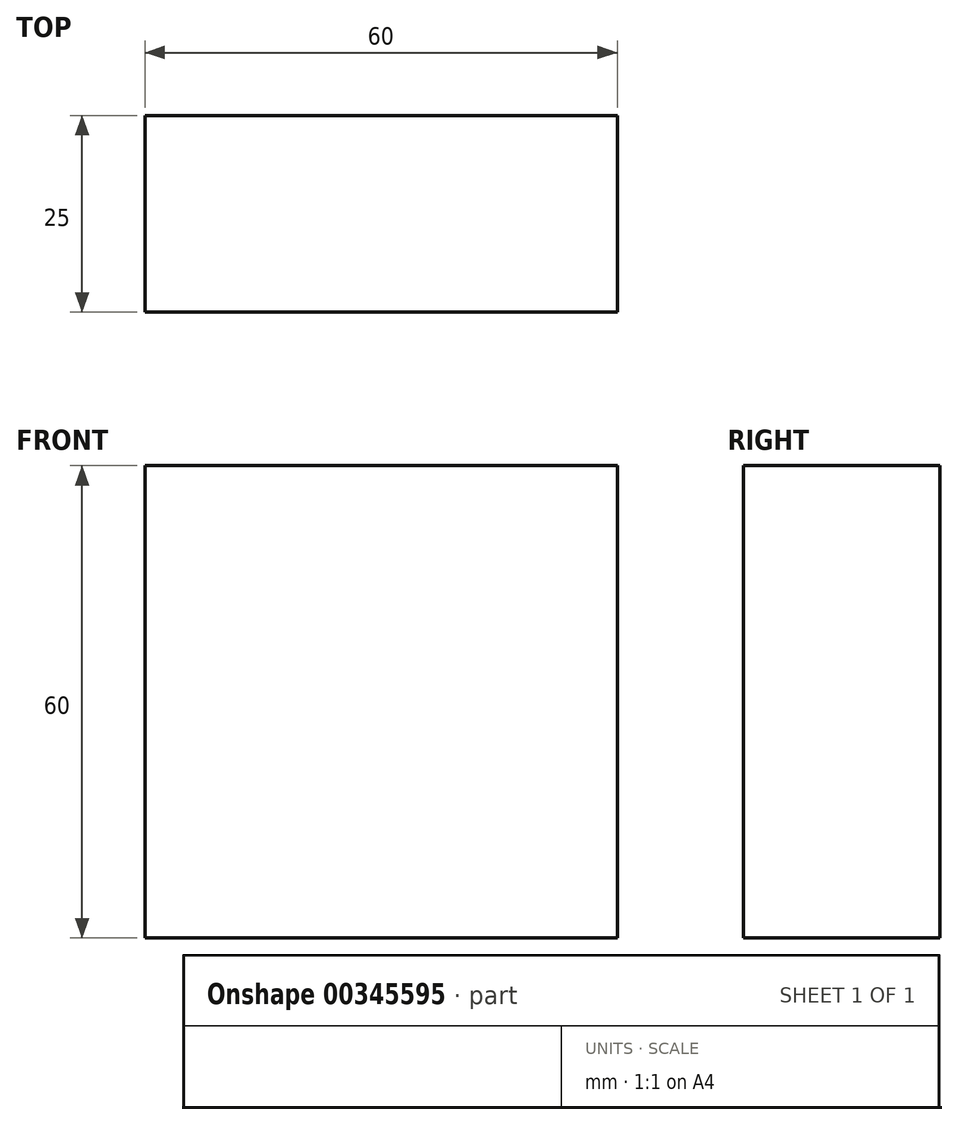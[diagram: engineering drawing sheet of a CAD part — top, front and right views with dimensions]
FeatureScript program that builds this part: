
annotation { "Feature Type Name" : "Feature", "Feature Type Description" : "" }
export const myFeature = defineFeature(function(context is Context, id is Id, definition is map)
    precondition{}
    {
        {
            var Q0;
            Q0=qCreatedBy(makeId("Front.planeOp"),FACE);
            var sketch = newSketch(context, id + "F0", { "sketchPlane" : qUnion([Q0])});
            skLineSegment(sketch, "E0.bottom", {"start": v(-28.85, 18.13) * mm, "end": v(31.15, 18.13) * mm});
            skLineSegment(sketch, "E0.top", {"start": v(-28.85, -41.87) * mm, "end": v(31.15, -41.87) * mm});
            skLineSegment(sketch, "E0.left", {"start": v(-28.85, 18.13) * mm, "end": v(-28.85, -41.87) * mm});
            skLineSegment(sketch, "E0.right", {"start": v(31.15, 18.13) * mm, "end": v(31.15, -41.87) * mm});
            skSolve(sketch);
        }
        {
            var Q0;
            Q0=qSketchRegion(id+"F0",true);
            extrude(context, id + "F1", {"entities" : qUnion([Q0]), "depth" : 25 * mm});
        }
        {
            var Q0;
            Q0=qCreatedBy(makeId("Front.planeOp"),FACE);
            var sketch = newSketch(context, id + "F2", { "sketchPlane" : qUnion([Q0])});
            skCircle(sketch, "E1", {"center": v(0, 14.94) * mm, "radius": 2.06 * mm});
            skPoint(sketch, "E2.center.orphan", {"position": v(0, 7.7) * mm});
            skSolve(sketch);
        }
        {
            var Q0;
            Q0=sQuery(id+"F2.wireOp",EDGE,"E1");
            extrude(context, id + "F3", {"bodyType" : ToolBodyType.SURFACE, "surfaceEntities" : qUnion([Q0]), "oppositeDirection" : true, "depth" : 250 * mm});
        }
    });
